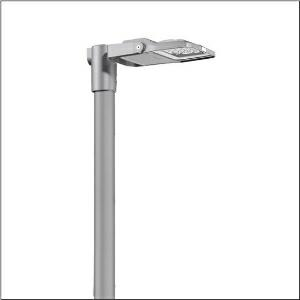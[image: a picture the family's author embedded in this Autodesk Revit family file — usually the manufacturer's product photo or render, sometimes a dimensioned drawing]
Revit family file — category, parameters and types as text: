
# Revit family: floodlight_fl_21_iq_micro___pl61_5xa7761a2c3a_df0f
name_source: partatom
category: Lighting Fixtures
units: mm (PartAtom-declared; Revit-internal decimal feet)

## family parameters
Cut with Voids When Loaded = No
Host = Face
Light Source = No
Part Type = Normal
Room Calculation Point = No
Round Connector Dimension = Use Diameter
Shared = No

## types (1)
- --- (1 x LED, 2910 lm, 23.1 W, 3000K)
    Apparent Load = 23 VA
    CIE Flux Codes = 33 65 98 100 100
    Color Rendering = 70
    Color Temperature = 3000K
    Default Elevation = 1800 mm
    Description = Floodlight FL 21 iQ micro, floodlight, primary light control with lens, of PMMA, primary optical cover: protective disc, of toughened safety glass, transparent, light distribution: PL61, light emission: direct distribution, installation type: surface-mounted, LED, High Power LED, rated luminous flux: 2.910lm, luminous efficacy: 126lm/W, light colour: 730, colour temperature: 3000K, control gear: iQ Comfort/DALI, control: optimised constant luminous flux control (CLO 2.0), Desk-Remote (wireless, voltage-free reading and setting of iQ features in the workshop via application-optimized NFC function/RFID function), Light-Fading, Smart-Wire, Night-Set, Lumen-Switch, Temp-Guard, Auto-Match, with terminal, 6-pole, mains connection: 220..240V, AC, 50/60Hz, start of lifetime: 23W, end of service life: 24W, reduction: 11W, luminaire housing, of diecast aluminium, powder-coated, Siteco® metallic grey (DB 702S), corrosivity category C5 mid according to DIN EN ISO 12944, suitable for swimming pools, chlorine-resistant, sealing non-destructively replaceable, please order mast flange separately, mast bracket, of steel, galvanised, powder-coated, Siteco® metallic grey (DB 702S), protection rating (complete): IP66, insulation class (complete): insulation class II (safety insulation), certification: CE, ENEC, VDE, protection symbol: D, impact resistance: IK07, permissible operating ambient temperature: -40..+40°C, permissible operating ambient temperature for outdoor applications: -40..+50°C, standard: DIN EN 12944, LABS conformity tested according to VDMA 24364:2018-05, packaging unit: 1 piece

Light Distribution: PL61
    Height = 65 mm
    Lamp = 1 x LED
    Lamp Light Flux = 2910 lm
    Lamp Power = 23.1 W
    Lamp count = 1
    Length = 312 mm
    Luminous efficacy = 126 lm/W
    Manufacturer = Siteco
    ModVariant = No
    Model = 5XA7761A2C3A
    Number of Poles = 1
    OnlyDefault = Yes
    Power Factor = 1
    Product Name = Floodlight FL 21 iQ micro | PL61
    Product group = floodlight | pylon top
    ProductGroupID = 6101
    Protection Class = Protection class II
    Protection Degree = IP 66
    RLX_Detail_Level = 1
    RLX_Emergency_Light_Flux = 0 lm
    RLX_Emergency_Type = 0
    RLX_Emergency_Type_DB = No
    RlxData = <blob elided: 101893 chars, md5=63ae9a1f>
    Socket = socket
    Standby Power = 0 W
    System Light Flux = 2910 lm
    System Power = 23 W
    Type Comments = factory setting: luminous flux: 100 % | dim-lin: 254 | 455 mA
    Type Image = l_1007121.jpg
    URL = http://relux.com
    VarID = @adj_194620
    Voltage = 0 V
    Weight = 0.00 kg
    Width = 230 mm

## geometry (parser evidence)
native form markers: Blend x4, Sweep x9
no freeform markers — native parametric forms only
